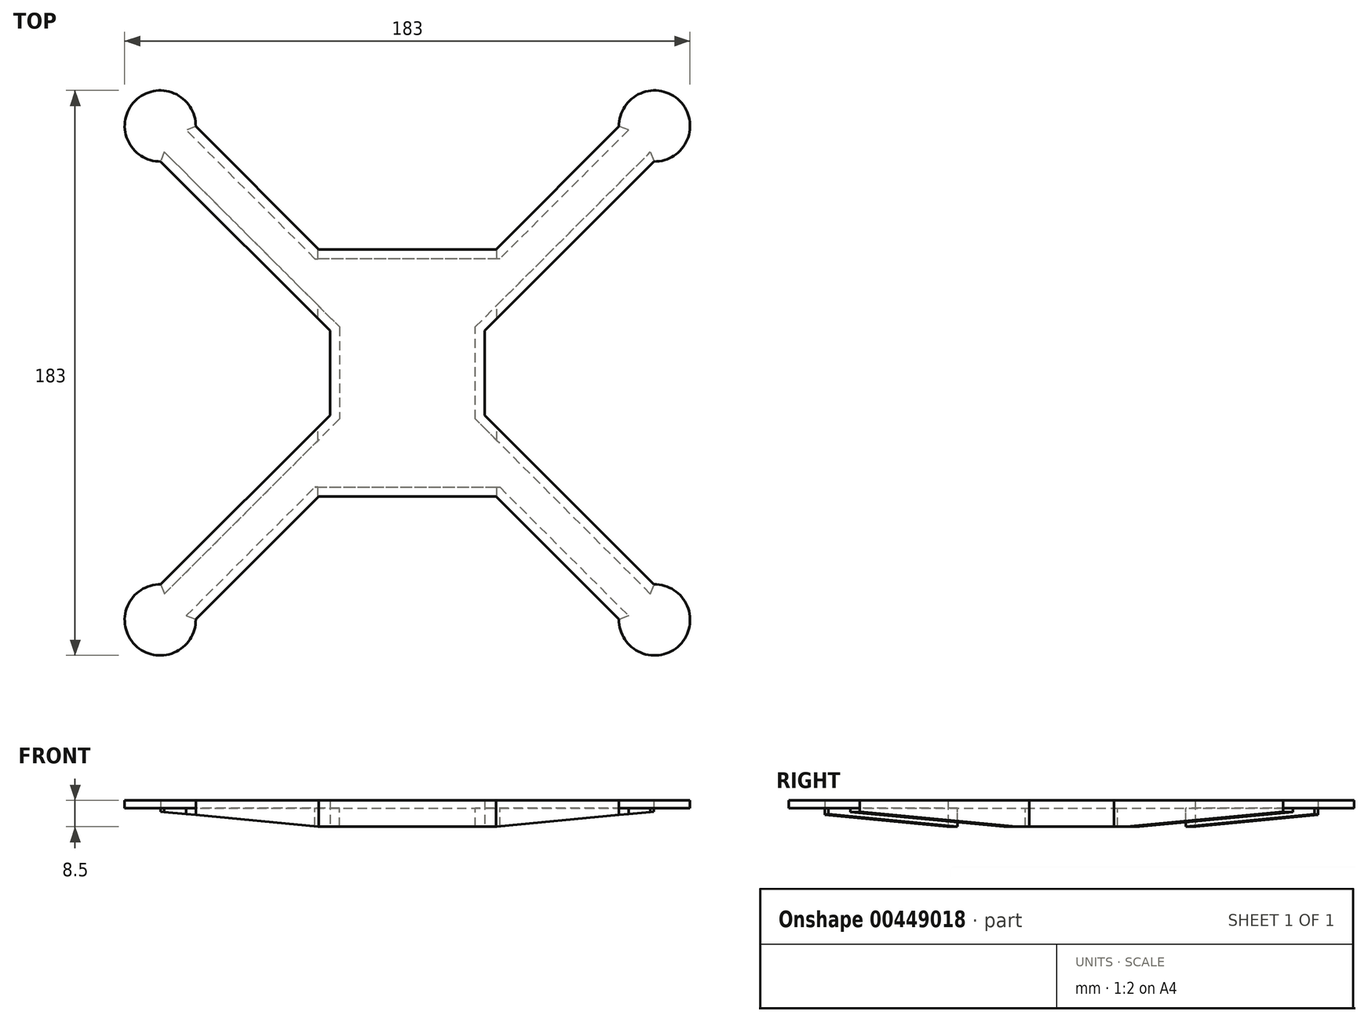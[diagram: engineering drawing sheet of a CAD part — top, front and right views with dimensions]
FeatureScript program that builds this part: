
annotation { "Feature Type Name" : "Feature", "Feature Type Description" : "" }
export const myFeature = defineFeature(function(context is Context, id is Id, definition is map)
    precondition{}
    {
        {
            var Q0;
            Q0=qCreatedBy(makeId("Top.planeOp"),FACE);
            var sketch = newSketch(context, id + "F0", { "sketchPlane" : qUnion([Q0])});
            skLineSegment(sketch, "E0.0", {"start": v(-25, 13.69) * mm, "end": v(-79.82, 68.5) * mm});
            skLineSegment(sketch, "E1.0", {"start": v(-28.69, 40) * mm, "end": v(-68.5, 79.82) * mm});
            skArc(sketch, "E2", {"start": v(-68.5, 79.82) * mm, "mid": v(-88.13, 88.13) * mm, "end": v(-79.82, 68.5) * mm});
            skArc(sketch, "E3.MirrorCS", {"start": v(-79.82, 68.5) * mm, "mid": v(-88.13, 88.13) * mm, "end": v(-68.5, 79.82) * mm});
            skLineSegment(sketch, "E4.MirrorCS", {"start": v(28.69, 40) * mm, "end": v(68.5, 79.82) * mm});
            skLineSegment(sketch, "E5.MirrorCS", {"start": v(25, 13.69) * mm, "end": v(79.82, 68.5) * mm});
            skArc(sketch, "E6.MirrorCS", {"start": v(79.82, 68.5) * mm, "mid": v(88.13, 88.13) * mm, "end": v(68.5, 79.82) * mm});
            skLineSegment(sketch, "E7.MirrorCS", {"start": v(-25, -13.69) * mm, "end": v(-79.82, -68.5) * mm});
            skLineSegment(sketch, "E8.MirrorCS", {"start": v(-28.69, -40) * mm, "end": v(-68.5, -79.82) * mm});
            skLineSegment(sketch, "E9.MirrorCS", {"start": v(28.69, -40) * mm, "end": v(68.5, -79.82) * mm});
            skLineSegment(sketch, "E10.MirrorCS", {"start": v(25, -13.69) * mm, "end": v(79.82, -68.5) * mm});
            skArc(sketch, "E11.MirrorCS", {"start": v(79.82, -68.5) * mm, "mid": v(88.13, -88.13) * mm, "end": v(68.5, -79.82) * mm});
            skArc(sketch, "E12.MirrorCS", {"start": v(-79.82, -68.5) * mm, "mid": v(-88.13, -88.13) * mm, "end": v(-68.5, -79.82) * mm});
            skLineSegment(sketch, "E13", {"start": v(-28.69, 40) * mm, "end": v(28.69, 40) * mm});
            skLineSegment(sketch, "E14.MirrorCS", {"start": v(-28.69, -40) * mm, "end": v(28.69, -40) * mm});
            skLineSegment(sketch, "E15", {"start": v(-25, 13.69) * mm, "end": v(-25, -13.69) * mm});
            skLineSegment(sketch, "E16.MirrorCS", {"start": v(25, 13.69) * mm, "end": v(25, -13.69) * mm});
            skPoint(sketch, "E17.orphan", {"position": v(0, 11.31) * mm});
            skPoint(sketch, "E18.orphan", {"position": v(-11.31, 0) * mm});
            skPoint(sketch, "E19.orphan", {"position": v(11.31, 0) * mm});
            skPoint(sketch, "E20.orphan", {"position": v(0, -11.31) * mm});
            skSolve(sketch);
        }
        {
            var Q0;
            Q0 = qSketchRegion(id + "F0", true);
            extrude(context, id + "F1", {"entities" : qUnion([Q0]), "depth" : 2.5 * mm});
        }
        {
            var Q0;
            Q0=qCreatedBy(makeId("Top.planeOp"),FACE);
            var sketch = newSketch(context, id + "F2", { "sketchPlane" : qUnion([Q0])});
            skLineSegment(sketch, "E21.0", {"start": v(-71.6, -78.67) * mm, "end": v(-29.93, -37) * mm});
            skLineSegment(sketch, "E21.2", {"start": v(-22, -14.93) * mm, "end": v(-78.67, -71.6) * mm});
            skLineSegment(sketch, "E21.3", {"start": v(-22, 14.93) * mm, "end": v(-22, -14.93) * mm});
            skLineSegment(sketch, "E21.4", {"start": v(-78.67, 71.6) * mm, "end": v(-22, 14.93) * mm});
            skLineSegment(sketch, "E21.5", {"start": v(22, -14.93) * mm, "end": v(22, 14.93) * mm});
            skLineSegment(sketch, "E21.6", {"start": v(78.67, -71.6) * mm, "end": v(22, -14.93) * mm});
            skLineSegment(sketch, "E21.8", {"start": v(29.93, -37) * mm, "end": v(71.6, -78.67) * mm});
            skLineSegment(sketch, "E21.9", {"start": v(22, 14.93) * mm, "end": v(78.67, 71.6) * mm});
            skLineSegment(sketch, "E21.11", {"start": v(71.6, 78.67) * mm, "end": v(29.93, 37) * mm});
            skLineSegment(sketch, "E21.12", {"start": v(29.93, 37) * mm, "end": v(-29.93, 37) * mm});
            skLineSegment(sketch, "E21.13", {"start": v(-29.93, 37) * mm, "end": v(-71.6, 78.67) * mm});
            skLineSegment(sketch, "E21.14", {"start": v(-29.93, -37) * mm, "end": v(29.93, -37) * mm});
            skLineSegment(sketch, "E22.0", {"start": v(-68.5, -79.82) * mm, "end": v(-28.69, -40) * mm});
            skLineSegment(sketch, "E22.2", {"start": v(-25, -13.69) * mm, "end": v(-79.82, -68.5) * mm});
            skLineSegment(sketch, "E22.3", {"start": v(-25, 13.69) * mm, "end": v(-25, -13.69) * mm});
            skLineSegment(sketch, "E22.4", {"start": v(-79.82, 68.5) * mm, "end": v(-25, 13.69) * mm});
            skLineSegment(sketch, "E22.5", {"start": v(25, -13.69) * mm, "end": v(25, 13.69) * mm});
            skLineSegment(sketch, "E22.6", {"start": v(79.82, -68.5) * mm, "end": v(25, -13.69) * mm});
            skLineSegment(sketch, "E22.8", {"start": v(28.69, -40) * mm, "end": v(68.5, -79.82) * mm});
            skLineSegment(sketch, "E22.9", {"start": v(25, 13.69) * mm, "end": v(79.82, 68.5) * mm});
            skLineSegment(sketch, "E22.11", {"start": v(68.5, 79.82) * mm, "end": v(28.69, 40) * mm});
            skLineSegment(sketch, "E22.12", {"start": v(28.69, 40) * mm, "end": v(-28.69, 40) * mm});
            skLineSegment(sketch, "E22.13", {"start": v(-28.69, 40) * mm, "end": v(-68.5, 79.82) * mm});
            skLineSegment(sketch, "E22.14", {"start": v(-28.69, -40) * mm, "end": v(28.69, -40) * mm});
            skLineSegment(sketch, "E23", {"start": v(-79.82, -68.5) * mm, "end": v(-78.67, -71.6) * mm});
            skLineSegment(sketch, "E24", {"start": v(-71.6, -78.67) * mm, "end": v(-68.5, -79.82) * mm});
            skLineSegment(sketch, "E25", {"start": v(78.67, -71.6) * mm, "end": v(79.82, -68.5) * mm});
            skLineSegment(sketch, "E26", {"start": v(71.6, -78.67) * mm, "end": v(68.5, -79.82) * mm});
            skLineSegment(sketch, "E27", {"start": v(78.67, 71.6) * mm, "end": v(79.82, 68.5) * mm});
            skLineSegment(sketch, "E28", {"start": v(71.6, 78.67) * mm, "end": v(68.5, 79.82) * mm});
            skLineSegment(sketch, "E29", {"start": v(-68.5, 79.82) * mm, "end": v(-71.6, 78.67) * mm});
            skLineSegment(sketch, "E30", {"start": v(-78.67, 71.6) * mm, "end": v(-79.82, 68.5) * mm});
            skSolve(sketch);
        }
        {
            var Q0;
            Q0 = qSketchRegion(id + "F2", true);
            extrude(context, id + "F3", {"entities" : qUnion([Q0]), "operationType" : NewBodyOperationType.ADD, "oppositeDirection" : true, "depth" : 6 * mm});
        }
        {
            var Q0;
            Q0=qCreatedBy(makeId("Front.planeOp"),FACE);
            var sketch = newSketch(context, id + "F4", { "sketchPlane" : qUnion([Q0])});
            skLineSegment(sketch, "E31", {"start": v(-28.7, -6.03) * mm, "end": v(-91.46, 0) * mm});
            skLineSegment(sketch, "E32", {"start": v(-91.46, 0) * mm, "end": v(-91.46, -15.8) * mm});
            skLineSegment(sketch, "E33", {"start": v(-91.46, -15.8) * mm, "end": v(-28.7, -15.8) * mm});
            skLineSegment(sketch, "E34", {"start": v(-28.7, -15.8) * mm, "end": v(-28.7, -6.03) * mm});
            skLineSegment(sketch, "E35.MirrorCS", {"start": v(28.7, -15.8) * mm, "end": v(28.7, -6.03) * mm});
            skLineSegment(sketch, "E36.MirrorCS", {"start": v(91.46, -15.8) * mm, "end": v(28.7, -15.8) * mm});
            skLineSegment(sketch, "E37.MirrorCS", {"start": v(28.7, -6.03) * mm, "end": v(91.46, 0) * mm});
            skLineSegment(sketch, "E38.MirrorCS", {"start": v(91.46, 0) * mm, "end": v(91.46, -15.8) * mm});
            skSolve(sketch);
        }
        {
            var Q0;
            Q0=makeQuery(id+"F4.imprint","IMPRINT",FACE,{"disambiguationData":[TD([[makeQuery(id+"F4.imprint","IMPRINT",EDGE,{"derivedFrom":sQuery(id+"F4.wireOp",EDGE,"E31")}),1.0]])]});
            var Q1;
            Q1=makeQuery(id+"F4.imprint","IMPRINT",FACE,{"disambiguationData":[TD([[makeQuery(id+"F4.imprint","IMPRINT",EDGE,{"derivedFrom":sQuery(id+"F4.wireOp",EDGE,"E35.MirrorCS")}),-1.0]])]});
            extrude(context, id + "F5", {"entities" : qUnion([Q0, Q1]), "operationType" : NewBodyOperationType.REMOVE, "endBound" : BoundingType.SYMMETRIC, "oppositeDirection" : true, "depth" : 200 * mm});
        }
    });
